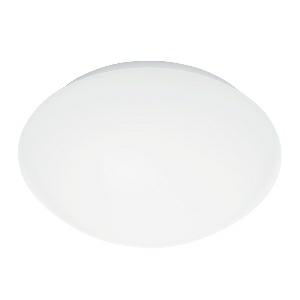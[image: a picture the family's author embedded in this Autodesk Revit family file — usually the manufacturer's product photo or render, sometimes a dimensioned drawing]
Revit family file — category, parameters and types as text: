
# Revit family: rs_pro_led_p2_056070
name_source: partatom
category: Leuchten
revit_build: Autodesk Revit 2016 (Build: 20190508_0715(x64)
units: mm (PartAtom-declared; Revit-internal decimal feet)

## family parameters
Basisbauteil = Fläche
Beim Laden mit Abzugskörper schneiden = Nein
Bemaßung runder Anschluss = Durchmesser verwenden
Gemeinsam genutzt = Nein
Lichtquelle = Nein
Raumberechnungspunkt = Nein
Teiletyp = Normal

## types (1)
- RS PRO LED P2 (1 x , 1810 lm, 4000 K)
    Beschreibung = Dimensions (Ø x H): 320 x 110 mm; Mains power supply: 220 – 240 V / 50 – 60 Hz; Sensor Technology: High frequency; Transmitter power: < 1 mW; HF-system: 5,8 GHz; Output: 16 W; Interconnection: Yes; Type of interconnection: Master/master; Luminous flux: 1810 lm; Colour temperature: 4000 K; Colour variation LED: SDCM3; Colour Rendering Index CRI: 80-89; With lamp: Yes, STEINEL LED system; Lamp: LED cannot be replaced; LED life expectancy (max. °C): 50000 h; Drop in luminous flux in accordance with LM80: L80B10; Base: without; LED cooling system: Passive Thermo Control; With motion detector: Yes; Detection: also through glass, wood and stud walls; Detection angle: 360 °; Angle of aperture: 160 °; Capability of masking out individual segments: Yes; Electronic scalability: Yes; Mechanical scalability: No; Reach, radial: Ø 8 m (50 m²); Reach, tangential: Ø 8 m (50 m²); Continuous light: selectable, 4h; Photo-cell controller: Yes; Twilight setting: 2 – 2000 lx; Time setting: 5 sec – 15 min; Basic light level function: Yes; Basic light level function time: 10/30 min, all night; Soft light start: Yes; Impact resistance: IK03; IP-rating: IP54; Protection class: II; Ambient temperature: 10 – 40 °C; Housing material: Plastic; Cover material: Plastic, opal; Manufacturer's Warranty: 5 years; Settings via: Potentiometers; With remote control: No; Version: Neutral white; PU1, EAN: 4007841056070
    CIE Flux Codes = 39 68 87 86 100
    Color Rendering = 80-89
    Color Temperature = 4000 K
    Frequency = 50 Hz, 60 Hz
    Height = 0 mm  [stored 0 ft]
    Hersteller = Steinel
    Lamp Light Flux = 1810 lm
    Lamp count = 1
    Lampe = 1 x
    Length = 320 mm
    Luminous efficacy = 113 lm/W
    ModVariant = Nein
    Modell = 056070
    Mounting Type = Surface mounted
    Number of Poles = 1
    OnlyDefault = Ja
    Power Factor = 1
    Product Name = RS PRO LED P2
    Product group = Sensor-switched indoor light
    ProductGroupID = 30
    Protection Class = Protection class II
    Protection Degree = IP 54
    RlxData = <blob elided: 37657 chars, md5=f0b22bcd>
    Scheinlast = 16 VA
    Socket = socket
    Standby Power = 0 W
    System Light Flux = 1810 lm
    System Power = 16 W
    Typenbild = produkt1_056070.jpg
    Typenkommentare = Product without accessories
    URL = http://relux.com
    VarID = ---
    Voltage = 0 V
    Vorgabe-Ansicht = 1800 mm
    Weight = 0.00 kg
    Width = 0 mm  [stored 0 ft]

note: [stored X ft] marks values corroborated as IEEE doubles in the binary element streams (Revit-internal decimal feet)

## geometry (parser evidence)
native form markers: Sweep x17
no freeform markers — native parametric forms only
